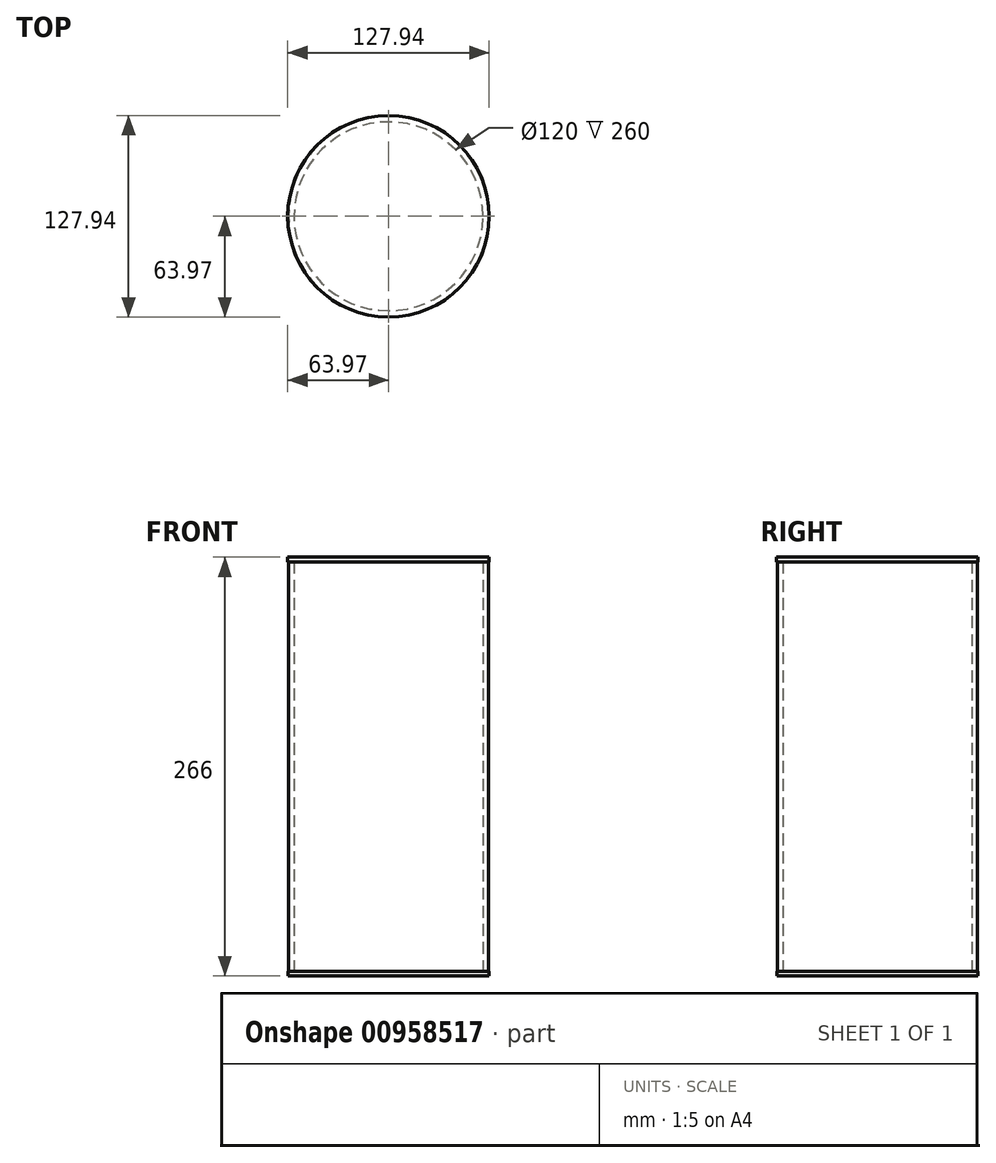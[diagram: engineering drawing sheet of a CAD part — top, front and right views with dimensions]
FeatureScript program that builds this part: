
annotation { "Feature Type Name" : "Feature", "Feature Type Description" : "" }
export const myFeature = defineFeature(function(context is Context, id is Id, definition is map)
    precondition{}
    {
        {
            var Q0;
            Q0=qCreatedBy(makeId("Top.planeOp"),FACE);
            var sketch = newSketch(context, id + "F0", { "sketchPlane" : qUnion([Q0])});
            skCircle(sketch, "E0", {"center": v(0, 0) * mm, "radius": 63.5 * mm});
            skCircle(sketch, "E1", {"center": v(0, 0) * mm, "radius": 60 * mm});
            skSolve(sketch);
        }
        {
            var Q0;
            Q0=makeQuery(id+"F0.imprint","IMPRINT",FACE,{"disambiguationData":[TD([[makeQuery(id+"F0.imprint","IMPRINT",EDGE,{"derivedFrom":sQuery(id+"F0.wireOp",EDGE,"E0")}),1.0]])]});
            extrude(context, id + "F1", {"entities" : qUnion([Q0]), "depth" : 260 * mm, "offsetDistance" : 25 * mm});
        }
        {
            var Q0;
            Q0=makeQuery(id+"F1.opExtrude","CAP_FACE",FACE,{"disambiguationData":[OSD([sQuery(id+"F0.wireOp",EDGE,"E0"),sQuery(id+"F0.wireOp",EDGE,"E1")])],"isStart":true});
            var sketch = newSketch(context, id + "F2", { "sketchPlane" : qUnion([Q0])});
            skCircle(sketch, "E2", {"center": v(0, 0) * mm, "radius": 63.8 * mm});
            skSolve(sketch);
        }
        {
            var Q0;
            Q0 = qSketchRegion(id + "F2", true);
            extrude(context, id + "F3", {"entities" : qUnion([Q0]), "operationType" : NewBodyOperationType.ADD, "depth" : 3 * mm, "offsetDistance" : 25 * mm});
        }
        {
            var Q0;
            Q0=makeQuery(id+"F1.opExtrude","CAP_FACE",FACE,{"disambiguationData":[OSD([sQuery(id+"F0.wireOp",EDGE,"E0"),sQuery(id+"F0.wireOp",EDGE,"E1")])],"isStart":false});
            var sketch = newSketch(context, id + "F4", { "sketchPlane" : qUnion([Q0])});
            skCircle(sketch, "E3", {"center": v(0, 0) * mm, "radius": 63.97 * mm});
            skSolve(sketch);
        }
        {
            var Q0;
            Q0 = qSketchRegion(id + "F4", true);
            extrude(context, id + "F5", {"entities" : qUnion([Q0]), "operationType" : NewBodyOperationType.ADD, "depth" : 3 * mm, "offsetDistance" : 25 * mm});
        }
    });
